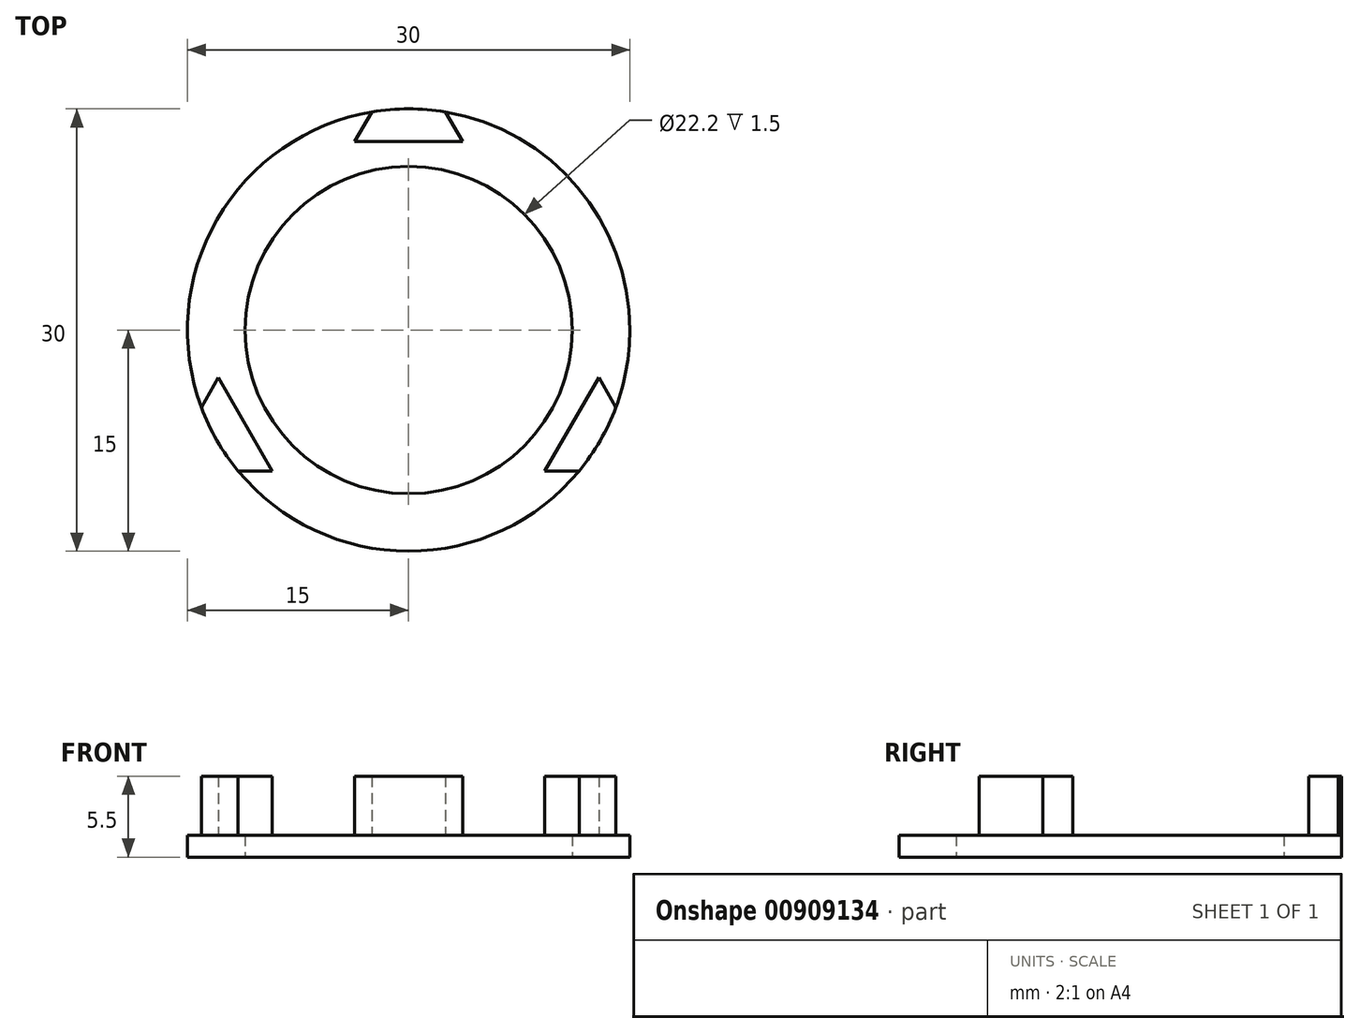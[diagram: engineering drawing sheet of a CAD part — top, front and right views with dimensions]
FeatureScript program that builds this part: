
annotation { "Feature Type Name" : "Feature", "Feature Type Description" : "" }
export const myFeature = defineFeature(function(context is Context, id is Id, definition is map)
    precondition{}
    {
        {
            var Q0;
            Q0=qCreatedBy(makeId("Top.planeOp"),FACE);
            var sketch = newSketch(context, id + "F0", { "sketchPlane" : qUnion([Q0])});
            skCircle(sketch, "E0", {"center": v(0, 0) * mm, "radius": 15 * mm});
            skCircle(sketch, "E1", {"center": v(0, 0) * mm, "radius": 11.1 * mm});
            skLineSegment(sketch, "E2.1", {"start": v(0, 12.78) * mm, "end": v(-3.65, 12.78) * mm});
            skLineSegment(sketch, "E2.2", {"start": v(0, 12.78) * mm, "end": v(3.65, 12.78) * mm});
            skLineSegment(sketch, "E3", {"start": v(-3.65, 12.78) * mm, "end": v(-2.5, 14.8) * mm});
            skLineSegment(sketch, "E4", {"start": v(3.65, 12.78) * mm, "end": v(2.5, 14.8) * mm});
            skSolve(sketch);
        }
        {
            var Q0;
            Q0=makeQuery(id+"F0.imprint","IMPRINT",FACE,{"disambiguationData":[TD([[makeQuery(id+"F0.imprint","IMPRINT",EDGE,{"derivedFrom":sQuery(id+"F0.wireOp",EDGE,"E1")}),-1.0]])]});
            var Q1;
            Q1=makeQuery(id+"F0.imprint","IMPRINT",FACE,{"disambiguationData":[TD([[makeQuery(id+"F0.imprint","IMPRINT",EDGE,{"derivedFrom":sQuery(id+"F0.wireOp",EDGE,"E2.1")}),-1.0]])]});
            extrude(context, id + "F1", {"entities" : qUnion([Q0, Q1]), "depth" : 1.5 * mm, "offsetDistance" : 25 * mm});
        }
        {
            var Q0;
            Q0=makeQuery(id+"F1.opExtrude","CAP_FACE",FACE,{"disambiguationData":[OSD([sQuery(id+"F0.wireOp",EDGE,"E0"),sQuery(id+"F0.wireOp",EDGE,"E1"),sQuery(id+"F0.wireOp",EDGE,"E2.1"),sQuery(id+"F0.wireOp",EDGE,"E2.2"),sQuery(id+"F0.wireOp",EDGE,"E3"),sQuery(id+"F0.wireOp",EDGE,"E4")])],"isStart":false});
            var sketch = newSketch(context, id + "F2", { "sketchPlane" : qUnion([Q0])});
            skLineSegment(sketch, "E5.MirrorCS", {"start": v(-9.24, 9.55) * mm, "end": v(-12.9, 3.23) * mm});
            skLineSegment(sketch, "E6.MirrorCS", {"start": v(-14.06, 5.24) * mm, "end": v(-12.9, 3.23) * mm});
            skLineSegment(sketch, "E7.MirrorCS", {"start": v(-11.56, 9.55) * mm, "end": v(-9.24, 9.55) * mm});
            skLineSegment(sketch, "E8.MirrorCS", {"start": v(9.24, 9.55) * mm, "end": v(12.9, 3.23) * mm});
            skLineSegment(sketch, "E9.MirrorCS", {"start": v(14.06, 5.24) * mm, "end": v(12.9, 3.23) * mm});
            skLineSegment(sketch, "E10.MirrorCS", {"start": v(11.56, 9.55) * mm, "end": v(9.24, 9.55) * mm});
            skLineSegment(sketch, "E11.MirrorCS", {"start": v(-9.24, -9.55) * mm, "end": v(-12.9, -3.23) * mm});
            skLineSegment(sketch, "E12.MirrorCS", {"start": v(-14.06, -5.24) * mm, "end": v(-12.9, -3.23) * mm});
            skLineSegment(sketch, "E13.MirrorCS", {"start": v(-11.56, -9.55) * mm, "end": v(-9.24, -9.55) * mm});
            skLineSegment(sketch, "E14.MirrorCS", {"start": v(9.24, -9.55) * mm, "end": v(12.9, -3.23) * mm});
            skLineSegment(sketch, "E15.MirrorCS", {"start": v(11.56, -9.55) * mm, "end": v(9.24, -9.55) * mm});
            skLineSegment(sketch, "E16.MirrorCS", {"start": v(14.06, -5.24) * mm, "end": v(12.9, -3.23) * mm});
            skSolve(sketch);
        }
        {
            var Q0;
            Q0=makeQuery(id+"F2.imprint","IMPRINT",FACE,{"disambiguationData":[TD([[makeQuery(id+"F2.imprint","IMPRINT",EDGE,{"derivedFrom":sQuery(id+"F2.wireOp",EDGE,"E14.MirrorCS")}),-1.0]])]});
            extrude(context, id + "F3", {"entities" : qUnion([Q0]), "depth" : 4 * mm, "offsetDistance" : 25 * mm});
        }
        {
            var Q0;
            Q0=makeQuery(id+"F3.opExtrude","SWEPT_BODY",BODY,{"disambiguationData":[OSD([sQuery(id+"F0.wireOp",EDGE,"E0"),sQuery(id+"F2.wireOp",EDGE,"E14.MirrorCS"),sQuery(id+"F2.wireOp",EDGE,"E15.MirrorCS"),sQuery(id+"F2.wireOp",EDGE,"E16.MirrorCS")])]});
            var Q1;
            Q1=sQuery(id+"F0.wireOp",EDGE,"E1");
            circularPattern(context, id + "F4", {"entities" : qUnion([Q0]), "axis" : qUnion([Q1]), "angle" : 360 * degree, "instanceCount" : 3, "equalSpace" : true});
        }
    });
